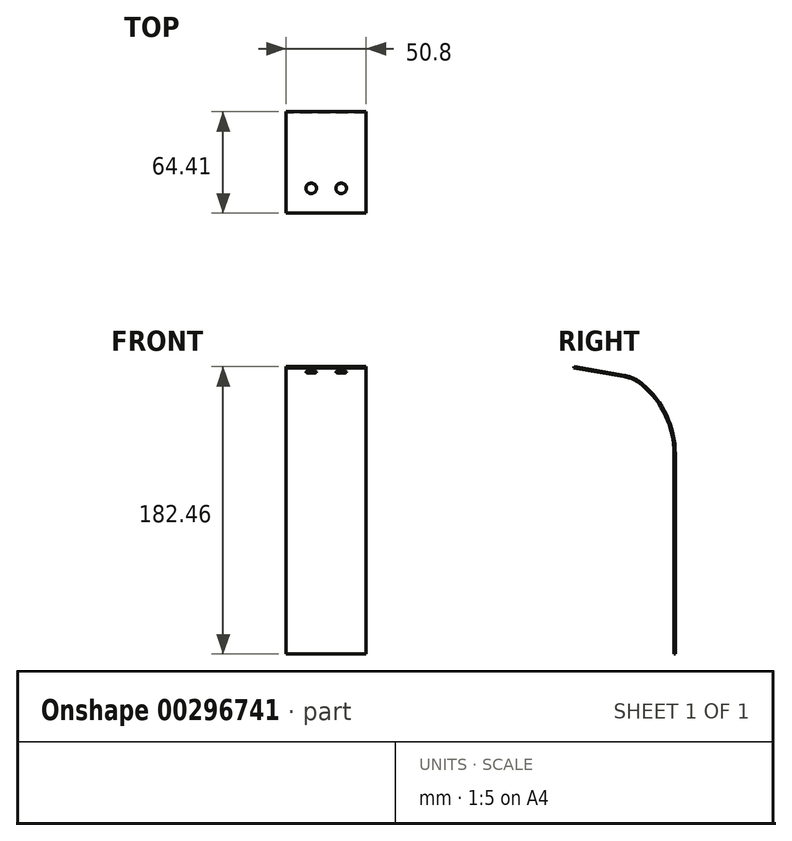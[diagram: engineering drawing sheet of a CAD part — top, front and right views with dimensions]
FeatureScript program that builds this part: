
annotation { "Feature Type Name" : "Feature", "Feature Type Description" : "" }
export const myFeature = defineFeature(function(context is Context, id is Id, definition is map)
    precondition{}
    {
        {
            var Q0;
            Q0=qCreatedBy(makeId("Top.planeOp"),FACE);
            var sketch = newSketch(context, id + "F0", { "sketchPlane" : qUnion([Q0])});
            skLineSegment(sketch, "E0.bottom", {"start": v(25.4, -0.4) * mm, "end": v(-25.4, -0.4) * mm});
            skLineSegment(sketch, "E0.top", {"start": v(25.4, 0.4) * mm, "end": v(-25.4, 0.4) * mm});
            skLineSegment(sketch, "E0.left", {"start": v(25.4, -0.4) * mm, "end": v(25.4, 0.4) * mm});
            skLineSegment(sketch, "E0.right", {"start": v(-25.4, -0.4) * mm, "end": v(-25.4, 0.4) * mm});
            skPoint(sketch, "E0.middle", {"position": v(0, 0) * mm});
            skSolve(sketch);
        }
        {
            var Q0;
            Q0=qCreatedBy(makeId("Right.planeOp"),FACE);
            var sketch = newSketch(context, id + "F1", { "sketchPlane" : qUnion([Q0])});
            skArc(sketch, "E1", {"start": v(0, 127) * mm, "mid": v(-5.4, 151.32) * mm, "end": v(-20.56, 171.08) * mm});
            skLineSegment(sketch, "E2", {"start": v(0, 0) * mm, "end": v(0, 127) * mm});
            skLineSegment(sketch, "E3", {"start": v(-32.08, 176.45) * mm, "end": v(-63.95, 182.07) * mm});
            skLineSegment(sketch, "E4", {"start": v(-20.56, 171.08) * mm, "end": v(-57.54, 127) * mm, "construction": true});
            skLineSegment(sketch, "E5", {"start": v(0, 127) * mm, "end": v(-57.54, 127) * mm, "construction": true});
            skLineSegment(sketch, "E6", {"start": v(-20.56, 171.08) * mm, "end": v(-45.91, 192.36) * mm, "construction": true});
            skArc(sketch, "E7", {"start": v(-20.56, 171.08) * mm, "mid": v(-25.96, 174.53) * mm, "end": v(-32.08, 176.45) * mm});
            skLineSegment(sketch, "E8", {"start": v(-63.95, 182.07) * mm, "end": v(-78.86, 97.53) * mm, "construction": true});
            skSolve(sketch);
        }
        {
            var Q0;
            Q0 = qSketchRegion(id + "F0", true);
            var Q1;
            Q1 = qConstructionFilter(qBodyType(qCreatedBy(id + "F1" ,EDGE), BodyType.WIRE), ConstructionObject.NO);
            sweep(context, id + "F2", {"profiles" : qUnion([Q0]), "path" : qUnion([Q1])});
        }
        {
            var Q0;
            Q0=makeQuery(id+"F2.opSweep","SWEPT_FACE",FACE,{"disambiguationData":[OSD([sQuery(id+"F0.wireOp",EDGE,"E0.top"),sQuery(id+"F1.wireOp",EDGE,"E3")])]});
            var sketch = newSketch(context, id + "F3", { "sketchPlane" : qUnion([Q0])});
            skLineSegment(sketch, "E9", {"start": v(-9.52, -78.72) * mm, "end": v(9.52, -78.72) * mm, "construction": true});
            skLineSegment(sketch, "E10", {"start": v(0, -78.72) * mm, "end": v(0, -94.6) * mm, "construction": true});
            skCircle(sketch, "E11", {"center": v(-9.52, -78.72) * mm, "radius": 3.37 * mm});
            skCircle(sketch, "E12", {"center": v(9.52, -78.72) * mm, "radius": 3.37 * mm});
            skSolve(sketch);
        }
        {
            var Q0;
            Q0 = qSketchRegion(id + "F3", true);
            extrude(context, id + "F4", {"entities" : qUnion([Q0]), "operationType" : NewBodyOperationType.REMOVE, "oppositeDirection" : true, "depth" : 25.4 * mm});
        }
    });
